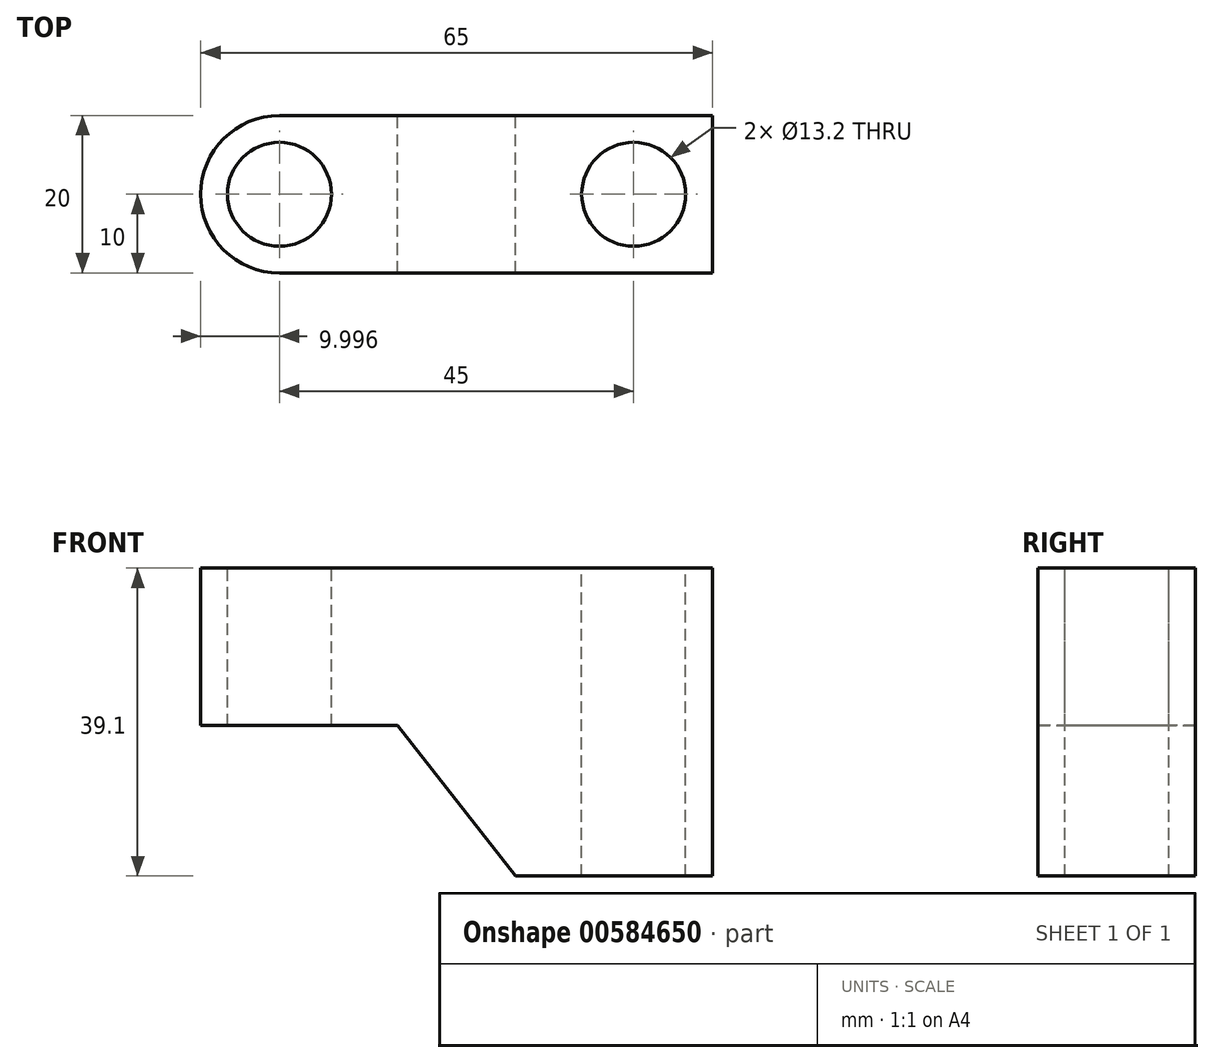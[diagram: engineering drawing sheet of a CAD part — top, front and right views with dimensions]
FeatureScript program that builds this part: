
annotation { "Feature Type Name" : "Feature", "Feature Type Description" : "" }
export const myFeature = defineFeature(function(context is Context, id is Id, definition is map)
    precondition{}
    {
        {
            var Q0;
            Q0=qCreatedBy(makeId("Front.planeOp"),FACE);
            var sketch = newSketch(context, id + "F0", { "sketchPlane" : qUnion([Q0])});
            skLineSegment(sketch, "E0", {"start": v(-18.9, 6.56) * mm, "end": v(-18.9, -13.44) * mm});
            skLineSegment(sketch, "E1", {"start": v(-18.9, -13.44) * mm, "end": v(6.1, -13.44) * mm});
            skLineSegment(sketch, "E2", {"start": v(6.1, -13.44) * mm, "end": v(21.1, -32.54) * mm});
            skLineSegment(sketch, "E3", {"start": v(21.1, -32.54) * mm, "end": v(46.1, -32.54) * mm});
            skLineSegment(sketch, "E4", {"start": v(46.1, -32.54) * mm, "end": v(46.1, 6.56) * mm});
            skLineSegment(sketch, "E5", {"start": v(46.1, 6.56) * mm, "end": v(-18.9, 6.56) * mm});
            skSolve(sketch);
        }
        {
            var Q0;
            Q0 = qSketchRegion(id + "F0", true);
            extrude(context, id + "F1", {"entities" : qUnion([Q0]), "depth" : 20 * mm, "offsetDistance" : 25 * mm});
        }
        {
            var Q0;
            Q0=makeQuery(id+"F1.opExtrude","CAP_EDGE",EDGE,{"disambiguationData":[OSD([sQuery(id+"F0.wireOp",EDGE,"E0")])],"isStart":true});
            var Q1;
            Q1=makeQuery(id+"F1.opExtrude","CAP_EDGE",EDGE,{"disambiguationData":[OSD([sQuery(id+"F0.wireOp",EDGE,"E0")])],"isStart":false});
            fillet(context, id + "F2", {"entities" : qUnion([Q0, Q1]), "radius" : 10 * mm, "tangentPropagation" : true, "allowEdgeOverflow" : false});
        }
        {
            var Q0;
            Q0=makeQuery(id+"F1.opExtrude","SWEPT_FACE",FACE,{"disambiguationData":[OSD([sQuery(id+"F0.wireOp",EDGE,"E5")])]});
            var sketch = newSketch(context, id + "F3", { "sketchPlane" : qUnion([Q0])});
            skPoint(sketch, "E6", {"position": v(-8.9, -10) * mm});
            skPoint(sketch, "E7", {"position": v(36.1, -10) * mm});
            skSolve(sketch);
        }
        {
            var Q0;
            Q0=sQuery(id+"F3.wireOp",VERTEX,"E6");
            var Q1;
            Q1=sQuery(id+"F3.wireOp",VERTEX,"E7");
            var Q2;
            Q2=makeQuery(id+"F1.opExtrude","SWEPT_BODY",BODY,{"disambiguationData":[OSD([sQuery(id+"F0.wireOp",EDGE,"E0"),sQuery(id+"F0.wireOp",EDGE,"E1"),sQuery(id+"F0.wireOp",EDGE,"E2"),sQuery(id+"F0.wireOp",EDGE,"E3"),sQuery(id+"F0.wireOp",EDGE,"E4"),sQuery(id+"F0.wireOp",EDGE,"E5")])]});
            hole(context, id + "F4", {"style" : HoleStyle.C_BORE, "endStyle" : HoleEndStyle.THROUGH, "holeDiameter" : 13.2 * mm, "cBoreDiameter" : 19.25 * mm, "cBoreDepth" : 0 * mm, "majorDiameter" : 5 * mm, "isTappedThrough" : true, "tappedDepth" : 12 * mm, "tapClearance" : 3, "startFromSketch" : true, "locations" : qUnion([Q0, Q1]), "scope" : qUnion([Q2])});
        }
    });
